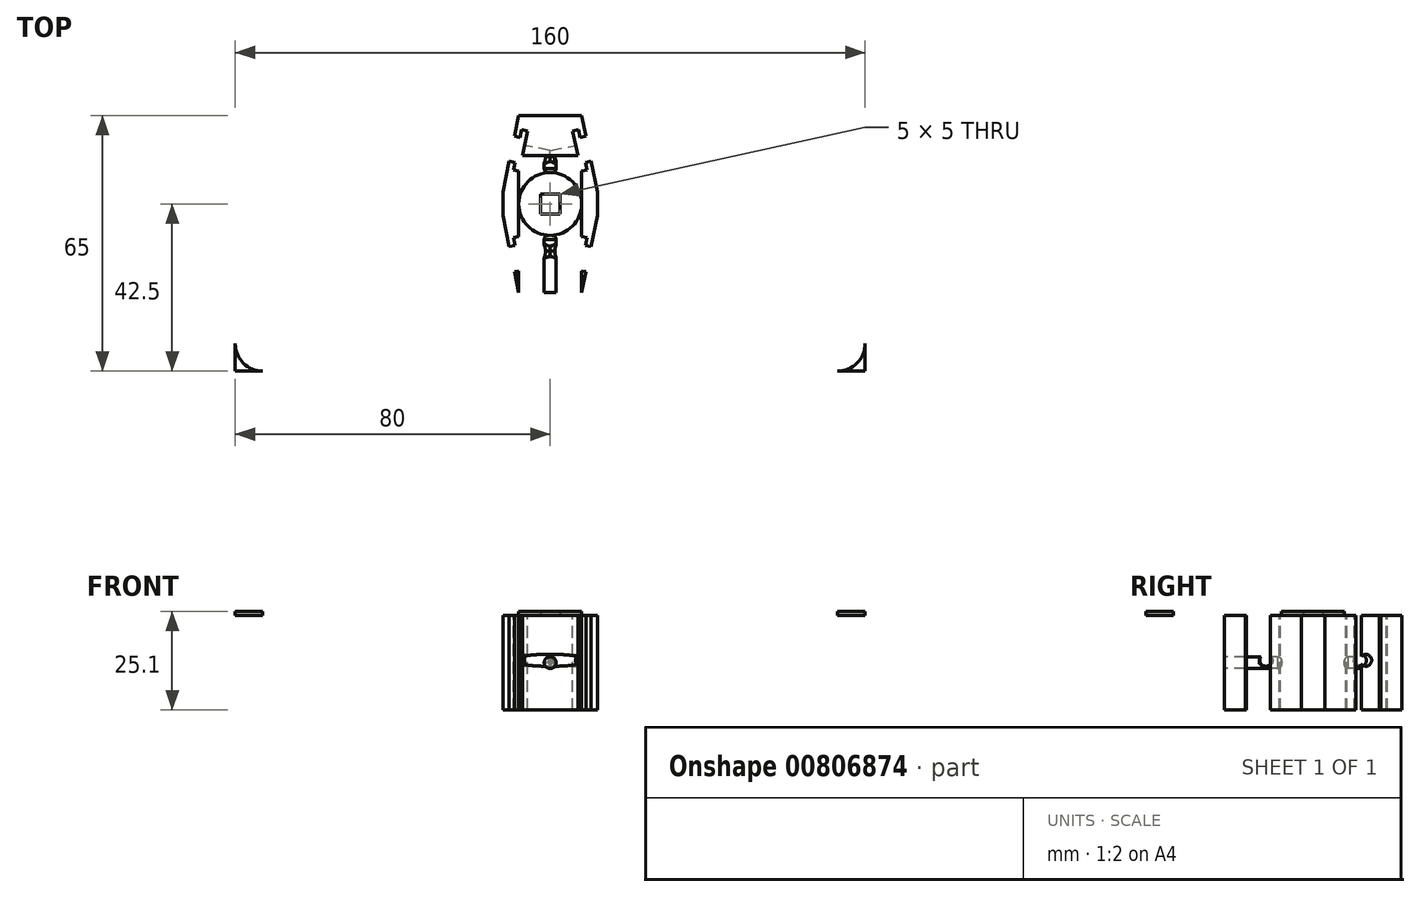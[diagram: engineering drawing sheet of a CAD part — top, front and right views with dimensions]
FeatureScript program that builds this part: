
annotation { "Feature Type Name" : "Feature", "Feature Type Description" : "" }
export const myFeature = defineFeature(function(context is Context, id is Id, definition is map)
    precondition{}
    {
        {
            var Q0;
            Q0=qCreatedBy(makeId("Top.planeOp"),FACE);
            var sketch = newSketch(context, id + "F0", { "sketchPlane" : qUnion([Q0])});
            skLineSegment(sketch, "E0.bottom", {"start": v(80, -42.5) * mm, "end": v(-80, -42.5) * mm});
            skLineSegment(sketch, "E0.top", {"start": v(80, 42.5) * mm, "end": v(-80, 42.5) * mm});
            skLineSegment(sketch, "E0.left", {"start": v(80, -42.5) * mm, "end": v(80, 42.5) * mm});
            skLineSegment(sketch, "E0.right", {"start": v(-80, -42.5) * mm, "end": v(-80, 42.5) * mm});
            skPoint(sketch, "E0.middle", {"position": v(0, 0) * mm});
            skCircle(sketch, "E1", {"center": v(0, 0) * mm, "radius": 8 * mm});
            skLineSegment(sketch, "E2", {"start": v(80, 42.5) * mm, "end": v(80, 35.5) * mm});
            skLineSegment(sketch, "E3", {"start": v(80, 42.5) * mm, "end": v(73, 42.5) * mm});
            skArc(sketch, "E4", {"start": v(80, 35.5) * mm, "mid": v(77.95, 40.45) * mm, "end": v(73, 42.5) * mm});
            skLineSegment(sketch, "E5", {"start": v(80, -42.5) * mm, "end": v(80, -35.5) * mm});
            skLineSegment(sketch, "E6", {"start": v(80, -42.5) * mm, "end": v(73, -42.5) * mm});
            skArc(sketch, "E7", {"start": v(73, -42.5) * mm, "mid": v(77.95, -40.45) * mm, "end": v(80, -35.5) * mm});
            skLineSegment(sketch, "E8", {"start": v(-80, -42.5) * mm, "end": v(-73, -42.5) * mm});
            skLineSegment(sketch, "E9", {"start": v(-80, -42.5) * mm, "end": v(-80, -35.5) * mm});
            skArc(sketch, "E10", {"start": v(-80, -35.5) * mm, "mid": v(-77.95, -40.45) * mm, "end": v(-73, -42.5) * mm});
            skLineSegment(sketch, "E11", {"start": v(-80, 42.5) * mm, "end": v(-80, 35.5) * mm});
            skLineSegment(sketch, "E12", {"start": v(-80, 42.5) * mm, "end": v(-73, 42.5) * mm});
            skArc(sketch, "E13", {"start": v(-73, 42.5) * mm, "mid": v(-77.95, 40.45) * mm, "end": v(-80, 35.5) * mm});
            skSolve(sketch);
        }
        {
            var Q0;
            Q0=makeQuery(id+"F0.imprint","IMPRINT",FACE,{"disambiguationData":[TD([[makeQuery(id+"F0.imprint","IMPRINT",EDGE,{"derivedFrom":sQuery(id+"F0.wireOp",EDGE,"E1")}),1.0]])]});
            var Q1;
            Q1=makeQuery(id+"F0.imprint","IMPRINT",FACE,{"disambiguationData":[TD([[makeQuery(id+"F0.imprint","IMPRINT",EDGE,{"derivedFrom":sQuery(id+"F0.wireOp",EDGE,"E0.bottom")}),-1.0]])]});
            extrude(context, id + "F1", {"entities" : qUnion([Q0, Q1]), "depth" : 1 * mm, "offsetDistance" : 25 * mm});
        }
        {
            var Q0;
            Q0=makeQuery(id+"F1.opExtrude","CAP_FACE",FACE,{"disambiguationData":[OSD([sQuery(id+"F0.wireOp",EDGE,"E0.bottom"),sQuery(id+"F0.wireOp",EDGE,"E0.top"),sQuery(id+"F0.wireOp",EDGE,"E0.left"),sQuery(id+"F0.wireOp",EDGE,"E0.right")])],"isStart":true});
            var sketch = newSketch(context, id + "F2", { "sketchPlane" : qUnion([Q0])});
            skCircle(sketch, "E14", {"center": v(0, 0) * mm, "radius": 8 * mm});
            skSolve(sketch);
        }
        {
            var Q0;
            Q0=makeQuery(id+"F1.opExtrude","CAP_FACE",FACE,{"disambiguationData":[OSD([sQuery(id+"F0.wireOp",EDGE,"E0.bottom"),sQuery(id+"F0.wireOp",EDGE,"E0.top"),sQuery(id+"F0.wireOp",EDGE,"E0.left"),sQuery(id+"F0.wireOp",EDGE,"E0.right")])],"isStart":true});
            var sketch = newSketch(context, id + "F3", { "sketchPlane" : qUnion([Q0])});
            skLineSegment(sketch, "E15", {"start": v(80, -42.5) * mm, "end": v(80, -3) * mm});
            skLineSegment(sketch, "E16", {"start": v(80, 42.5) * mm, "end": v(80, 3) * mm});
            skLineSegment(sketch, "E17", {"start": v(-80, 42.5) * mm, "end": v(-80, 3) * mm});
            skLineSegment(sketch, "E18", {"start": v(-80, -42.5) * mm, "end": v(-80, -3) * mm});
            skLineSegment(sketch, "E19", {"start": v(-80, 3) * mm, "end": v(-12, 3) * mm});
            skLineSegment(sketch, "E20", {"start": v(-80, -3) * mm, "end": v(-12, -3) * mm});
            skLineSegment(sketch, "E21", {"start": v(80, 3) * mm, "end": v(12, 3) * mm});
            skLineSegment(sketch, "E22", {"start": v(80, -3) * mm, "end": v(12, -3) * mm});
            skLineSegment(sketch, "E23", {"start": v(-12, 3) * mm, "end": v(-12, -3) * mm});
            skLineSegment(sketch, "E24", {"start": v(12, 3) * mm, "end": v(12, -3) * mm});
            skLineSegment(sketch, "E25", {"start": v(-8, -42.5) * mm, "end": v(73, -42.5) * mm});
            skLineSegment(sketch, "E26", {"start": v(8, -42.5) * mm, "end": v(73, -42.5) * mm});
            skLineSegment(sketch, "E27", {"start": v(-8, 42.5) * mm, "end": v(73, 42.5) * mm});
            skLineSegment(sketch, "E28", {"start": v(8, 42.5) * mm, "end": v(73, 42.5) * mm});
            skLineSegment(sketch, "E29", {"start": v(-8, 42.5) * mm, "end": v(-8, 22.5) * mm});
            skLineSegment(sketch, "E30", {"start": v(8, 42.5) * mm, "end": v(8, 22.5) * mm});
            skLineSegment(sketch, "E31", {"start": v(-8, -42.5) * mm, "end": v(-8, -22.5) * mm});
            skLineSegment(sketch, "E32", {"start": v(8, -42.5) * mm, "end": v(8, -22.5) * mm});
            skLineSegment(sketch, "E33", {"start": v(-8, -22.5) * mm, "end": v(8, -22.5) * mm});
            skLineSegment(sketch, "E34", {"start": v(-8, 22.5) * mm, "end": v(8, 22.5) * mm});
            skLineSegment(sketch, "E35", {"start": v(8, 22.5) * mm, "end": v(12, 3) * mm});
            skLineSegment(sketch, "E36", {"start": v(12, -3) * mm, "end": v(8, -22.5) * mm});
            skLineSegment(sketch, "E37", {"start": v(-8, -22.5) * mm, "end": v(-12, -3) * mm});
            skLineSegment(sketch, "E38", {"start": v(-8, 22.5) * mm, "end": v(-12, 3) * mm});
            skLineSegment(sketch, "E39", {"start": v(12, 3) * mm, "end": v(11.2, 6.92) * mm});
            skLineSegment(sketch, "E40", {"start": v(12, 3) * mm, "end": v(10.4, 10.84) * mm});
            skLineSegment(sketch, "E41", {"start": v(12, 3) * mm, "end": v(9.09, 17.2) * mm});
            skLineSegment(sketch, "E42", {"start": v(12, 3) * mm, "end": v(9.39, 15.73) * mm});
            skLineSegment(sketch, "E43", {"start": v(9.09, 17.2) * mm, "end": v(7.62, 16.9) * mm});
            skLineSegment(sketch, "E44", {"start": v(7.62, 16.9) * mm, "end": v(7.22, 18.86) * mm});
            skLineSegment(sketch, "E45", {"start": v(7.22, 18.86) * mm, "end": v(5.75, 18.56) * mm});
            skLineSegment(sketch, "E46", {"start": v(10.4, 10.84) * mm, "end": v(8.92, 10.54) * mm});
            skLineSegment(sketch, "E47", {"start": v(8.92, 10.54) * mm, "end": v(9.32, 8.58) * mm});
            skLineSegment(sketch, "E48", {"start": v(9.32, 8.58) * mm, "end": v(7.86, 8.27) * mm});
            skLineSegment(sketch, "E49", {"start": v(7.86, 8.27) * mm, "end": v(5.75, 18.56) * mm});
            skLineSegment(sketch, "E50", {"start": v(-12, 3) * mm, "end": v(-11.2, 6.92) * mm});
            skLineSegment(sketch, "E51", {"start": v(-12, 3) * mm, "end": v(-10.4, 10.84) * mm});
            skLineSegment(sketch, "E52", {"start": v(-12, 3) * mm, "end": v(-9.09, 17.2) * mm});
            skLineSegment(sketch, "E53", {"start": v(-12, 3) * mm, "end": v(-9.39, 15.73) * mm});
            skLineSegment(sketch, "E54", {"start": v(-10.4, 10.84) * mm, "end": v(-8.92, 10.54) * mm});
            skLineSegment(sketch, "E55", {"start": v(-8.92, 10.54) * mm, "end": v(-9.32, 8.58) * mm});
            skLineSegment(sketch, "E56", {"start": v(-9.32, 8.58) * mm, "end": v(-7.86, 8.27) * mm});
            skLineSegment(sketch, "E57", {"start": v(-9.09, 17.2) * mm, "end": v(-7.62, 16.9) * mm});
            skLineSegment(sketch, "E58", {"start": v(-7.62, 16.9) * mm, "end": v(-7.22, 18.86) * mm});
            skLineSegment(sketch, "E59", {"start": v(-7.22, 18.86) * mm, "end": v(-5.75, 18.56) * mm});
            skLineSegment(sketch, "E60", {"start": v(-5.75, 18.56) * mm, "end": v(-7.86, 8.27) * mm});
            skLineSegment(sketch, "E61", {"start": v(12, -3) * mm, "end": v(10.8, -8.88) * mm});
            skLineSegment(sketch, "E62", {"start": v(12, -3) * mm, "end": v(10.4, -10.84) * mm});
            skLineSegment(sketch, "E63", {"start": v(12, -3) * mm, "end": v(9.09, -17.2) * mm});
            skLineSegment(sketch, "E64", {"start": v(12, -3) * mm, "end": v(8.99, -17.7) * mm});
            skLineSegment(sketch, "E65", {"start": v(10.4, -10.84) * mm, "end": v(8.92, -10.54) * mm});
            skLineSegment(sketch, "E66", {"start": v(8.92, -10.54) * mm, "end": v(9.32, -8.58) * mm});
            skLineSegment(sketch, "E67", {"start": v(9.32, -8.58) * mm, "end": v(7.86, -8.27) * mm});
            skLineSegment(sketch, "E68", {"start": v(9.09, -17.2) * mm, "end": v(7.62, -16.9) * mm});
            skLineSegment(sketch, "E69", {"start": v(7.62, -16.9) * mm, "end": v(7.22, -18.86) * mm});
            skLineSegment(sketch, "E70", {"start": v(7.22, -18.86) * mm, "end": v(5.75, -18.56) * mm});
            skLineSegment(sketch, "E71", {"start": v(5.75, -18.56) * mm, "end": v(7.86, -8.27) * mm});
            skLineSegment(sketch, "E72", {"start": v(-12, -3) * mm, "end": v(-11.2, -6.92) * mm});
            skLineSegment(sketch, "E73", {"start": v(-12, -3) * mm, "end": v(-10.4, -10.84) * mm});
            skLineSegment(sketch, "E74", {"start": v(-12, -3) * mm, "end": v(-9.09, -17.2) * mm});
            skLineSegment(sketch, "E75", {"start": v(-12, -3) * mm, "end": v(-9.39, -15.73) * mm});
            skLineSegment(sketch, "E76", {"start": v(-10.4, -10.84) * mm, "end": v(-8.92, -10.54) * mm});
            skLineSegment(sketch, "E77", {"start": v(-8.92, -10.54) * mm, "end": v(-9.32, -8.58) * mm});
            skLineSegment(sketch, "E78", {"start": v(-9.32, -8.58) * mm, "end": v(-7.86, -8.27) * mm});
            skLineSegment(sketch, "E79", {"start": v(-9.09, -17.2) * mm, "end": v(-7.62, -16.9) * mm});
            skLineSegment(sketch, "E80", {"start": v(-7.62, -16.9) * mm, "end": v(-7.22, -18.86) * mm});
            skLineSegment(sketch, "E81", {"start": v(-7.22, -18.86) * mm, "end": v(-5.75, -18.56) * mm});
            skLineSegment(sketch, "E82", {"start": v(-5.75, -18.56) * mm, "end": v(-7.86, -8.27) * mm});
            skCircle(sketch, "E83", {"center": v(0, 0) * mm, "radius": 8 * mm});
            skLineSegment(sketch, "E84", {"start": v(9.09, 17.2) * mm, "end": v(10.4, 10.84) * mm});
            skLineSegment(sketch, "E85", {"start": v(10.4, -10.84) * mm, "end": v(9.09, -17.2) * mm});
            skLineSegment(sketch, "E86", {"start": v(-10.4, -10.84) * mm, "end": v(-9.09, -17.2) * mm});
            skSolve(sketch);
        }
        {
            var Q0;
            {var subQ5=sQuery(id+"F3.wireOp",EDGE,"E23");Q0=makeQuery(id+"F3.imprint","IMPRINT",FACE,{"disambiguationData":[TD([[makeQuery(id+"F3.imprint","IMPRINT",EDGE,{"derivedFrom":subQ5}),1.0]])]});}
            extrude(context, id + "F4", {"entities" : qUnion([Q0]), "operationType" : NewBodyOperationType.ADD, "depth" : 24.1 * mm, "offsetDistance" : 25 * mm});
        }
        {
            var Q0;
            Q0=makeQuery(id+"F4.opExtrude","CAP_FACE",FACE,{"disambiguationData":[OSD([sQuery(id+"F3.wireOp",EDGE,"E23"),sQuery(id+"F3.wireOp",EDGE,"E24"),sQuery(id+"F3.wireOp",EDGE,"E33"),sQuery(id+"F3.wireOp",EDGE,"E34"),sQuery(id+"F3.wireOp",EDGE,"E35"),sQuery(id+"F3.wireOp",EDGE,"E36"),sQuery(id+"F3.wireOp",EDGE,"E37"),sQuery(id+"F3.wireOp",EDGE,"E38"),sQuery(id+"F3.wireOp",EDGE,"E42"),sQuery(id+"F3.wireOp",EDGE,"E43"),sQuery(id+"F3.wireOp",EDGE,"E44"),sQuery(id+"F3.wireOp",EDGE,"E45"),sQuery(id+"F3.wireOp",EDGE,"E46"),sQuery(id+"F3.wireOp",EDGE,"E47"),sQuery(id+"F3.wireOp",EDGE,"E48"),sQuery(id+"F3.wireOp",EDGE,"E49"),sQuery(id+"F3.wireOp",EDGE,"E53"),sQuery(id+"F3.wireOp",EDGE,"E54"),sQuery(id+"F3.wireOp",EDGE,"E55"),sQuery(id+"F3.wireOp",EDGE,"E56"),sQuery(id+"F3.wireOp",EDGE,"E57"),sQuery(id+"F3.wireOp",EDGE,"E58"),sQuery(id+"F3.wireOp",EDGE,"E59"),sQuery(id+"F3.wireOp",EDGE,"E60"),sQuery(id+"F3.wireOp",EDGE,"E64"),sQuery(id+"F3.wireOp",EDGE,"E65"),sQuery(id+"F3.wireOp",EDGE,"E66"),sQuery(id+"F3.wireOp",EDGE,"E67"),sQuery(id+"F3.wireOp",EDGE,"E68"),sQuery(id+"F3.wireOp",EDGE,"E69"),sQuery(id+"F3.wireOp",EDGE,"E70"),sQuery(id+"F3.wireOp",EDGE,"E71"),sQuery(id+"F3.wireOp",EDGE,"E75"),sQuery(id+"F3.wireOp",EDGE,"E76"),sQuery(id+"F3.wireOp",EDGE,"E77"),sQuery(id+"F3.wireOp",EDGE,"E78"),sQuery(id+"F3.wireOp",EDGE,"E79"),sQuery(id+"F3.wireOp",EDGE,"E80"),sQuery(id+"F3.wireOp",EDGE,"E81"),sQuery(id+"F3.wireOp",EDGE,"E82"),sQuery(id+"F3.wireOp",EDGE,"E83")])],"isStart":false});
            var sketch = newSketch(context, id + "F5", { "sketchPlane" : qUnion([Q0])});
            skLineSegment(sketch, "E87", {"start": v(8, -22.5) * mm, "end": v(-8, -22.5) * mm});
            skLineSegment(sketch, "E88", {"start": v(8, -22.5) * mm, "end": v(8.4, -20.54) * mm});
            skLineSegment(sketch, "E89", {"start": v(-8, -22.5) * mm, "end": v(-8.4, -20.54) * mm});
            skLineSegment(sketch, "E90", {"start": v(-8.4, -20.54) * mm, "end": v(8.4, -20.54) * mm});
            skSolve(sketch);
        }
        {
            var Q0;
            Q0=makeQuery(id+"F4.opExtrude","SWEPT_FACE",FACE,{"disambiguationData":[OSD([sQuery(id+"F3.wireOp",EDGE,"E71")])]});
            var sketch = newSketch(context, id + "F6", { "sketchPlane" : qUnion([Q0])});
            skLineSegment(sketch, "E91", {"start": v(11.78, 0) * mm, "end": v(11.78, -11.45) * mm});
            skCircle(sketch, "E92", {"center": v(11.78, -11.45) * mm, "radius": 1.5 * mm});
            skSolve(sketch);
        }
        {
            var Q0;
            Q0=makeQuery(id+"F6.imprint","IMPRINT",FACE,{"disambiguationData":[TD([[makeQuery(id+"F6.imprint","IMPRINT",EDGE,{"derivedFrom":sQuery(id+"F6.wireOp",EDGE,"E92")}),1.0]])]});
            var Q1;
            Q1=sQuery(id+"F6.wireOp",EDGE,"E92");
            extrude(context, id + "F7", {"entities" : qUnion([Q0]), "operationType" : NewBodyOperationType.REMOVE, "surfaceEntities" : qUnion([Q1]), "oppositeDirection" : true, "depth" : 8.71 * mm, "offsetDistance" : 25 * mm});
        }
        {
            var Q0;
            Q0=makeQuery(id+"F4.opExtrude","SWEPT_FACE",FACE,{"disambiguationData":[OSD([sQuery(id+"F3.wireOp",EDGE,"E82")])]});
            var sketch = newSketch(context, id + "F8", { "sketchPlane" : qUnion([Q0])});
            skLineSegment(sketch, "E93", {"start": v(-11.78, 0) * mm, "end": v(-11.78, -11.45) * mm});
            skCircle(sketch, "E94", {"center": v(-11.78, -11.45) * mm, "radius": 1.5 * mm});
            skSolve(sketch);
        }
        {
            var Q0;
            Q0=makeQuery(id+"F8.imprint","IMPRINT",FACE,{"disambiguationData":[TD([[makeQuery(id+"F8.imprint","IMPRINT",EDGE,{"derivedFrom":sQuery(id+"F8.wireOp",EDGE,"E94")}),1.0]])]});
            var Q1;
            Q1=sQuery(id+"F8.wireOp",EDGE,"E94");
            extrude(context, id + "F9", {"entities" : qUnion([Q0]), "operationType" : NewBodyOperationType.REMOVE, "surfaceEntities" : qUnion([Q1]), "oppositeDirection" : true, "depth" : 8.18 * mm, "offsetDistance" : 25 * mm});
        }
        {
            var Q0;
            Q0=makeQuery(id+"F4.opExtrude","SWEPT_FACE",FACE,{"disambiguationData":[OSD([sQuery(id+"F3.wireOp",EDGE,"E60")])]});
            var sketch = newSketch(context, id + "F10", { "sketchPlane" : qUnion([Q0])});
            skLineSegment(sketch, "E95", {"start": v(11.78, 0) * mm, "end": v(11.78, -11.45) * mm});
            skCircle(sketch, "E96", {"center": v(11.78, -11.45) * mm, "radius": 1.5 * mm});
            skSolve(sketch);
        }
        {
            var Q0;
            Q0=qSketchRegion(id+"F10",true);
            extrude(context, id + "F11", {"entities" : qUnion([Q0]), "operationType" : NewBodyOperationType.REMOVE, "oppositeDirection" : true, "depth" : 8.71 * mm, "offsetDistance" : 25 * mm});
        }
        {
            var Q0;
            Q0=makeQuery(id+"F4.opExtrude","SWEPT_FACE",FACE,{"disambiguationData":[OSD([sQuery(id+"F3.wireOp",EDGE,"E49")])]});
            var sketch = newSketch(context, id + "F12", { "sketchPlane" : qUnion([Q0])});
            skLineSegment(sketch, "E97", {"start": v(-11.78, 0) * mm, "end": v(-11.78, -11.45) * mm});
            skCircle(sketch, "E98", {"center": v(-11.78, -11.45) * mm, "radius": 1.5 * mm});
            skSolve(sketch);
        }
        {
            var Q0;
            Q0=qSketchRegion(id+"F12",true);
            extrude(context, id + "F13", {"entities" : qUnion([Q0]), "operationType" : NewBodyOperationType.REMOVE, "oppositeDirection" : true, "depth" : 8.71 * mm, "offsetDistance" : 25 * mm});
        }
        {
            var Q0;
            Q0=makeQuery(id+"F4.boolean.opBoolean","SPLIT",FACE,{"disambiguationData":[TD([makeQuery(id+"F4.opExtrude","SWEPT_FACE",FACE,{"disambiguationData":[OSD([sQuery(id+"F3.wireOp",EDGE,"E83")])]})])],"derivedFrom":makeQuery(id+"F1.opExtrude","CAP_FACE",FACE,{"disambiguationData":[OSD([sQuery(id+"F0.wireOp",EDGE,"E0.bottom"),sQuery(id+"F0.wireOp",EDGE,"E0.top"),sQuery(id+"F0.wireOp",EDGE,"E0.left"),sQuery(id+"F0.wireOp",EDGE,"E0.right")])],"isStart":true})});
            var sketch = newSketch(context, id + "F14", { "sketchPlane" : qUnion([Q0])});
            skLineSegment(sketch, "E99.bottom", {"start": v(2.5, -2.5) * mm, "end": v(-2.5, -2.5) * mm});
            skLineSegment(sketch, "E99.top", {"start": v(2.5, 2.5) * mm, "end": v(-2.5, 2.5) * mm});
            skLineSegment(sketch, "E99.left", {"start": v(2.5, -2.5) * mm, "end": v(2.5, 2.5) * mm});
            skLineSegment(sketch, "E99.right", {"start": v(-2.5, -2.5) * mm, "end": v(-2.5, 2.5) * mm});
            skPoint(sketch, "E99.middle", {"position": v(0, 0) * mm});
            skSolve(sketch);
        }
        {
            var Q0;
            Q0=qSketchRegion(id+"F14",true);
            extrude(context, id + "F15", {"entities" : qUnion([Q0]), "operationType" : NewBodyOperationType.REMOVE, "oppositeDirection" : true, "depth" : 25 * mm, "offsetDistance" : 25 * mm});
        }
        {
            var Q0;
            Q0=makeQuery(id+"F4.opExtrude","SWEPT_FACE",FACE,{"disambiguationData":[OSD([sQuery(id+"F3.wireOp",EDGE,"E34")])]});
            var sketch = newSketch(context, id + "F16", { "sketchPlane" : qUnion([Q0])});
            skLineSegment(sketch, "E100", {"start": v(0, -24.1) * mm, "end": v(0, 0) * mm});
            skLineSegment(sketch, "E101", {"start": v(0, 0) * mm, "end": v(0, -12.05) * mm});
            skCircle(sketch, "E102", {"center": v(0, -12.05) * mm, "radius": 1.5 * mm});
            skSolve(sketch);
        }
        {
            var Q0;
            {var subQ0=sQuery(id+"F16.wireOp",EDGE,"E101");var subQ1=sQuery(id+"F16.wireOp",EDGE,"E100");var subQ2=makeQuery(id+"F16.imprint","INTERSECT",VERTEX,{"derivedFrom":[subQ1,subQ0]});Q0=makeQuery(id+"F16.imprint","IMPRINT",FACE,{"disambiguationData":[TD([[makeQuery(id+"F16.imprint","IMPRINT",EDGE,{"disambiguationData":[TD([[subQ2,1.0]])],"derivedFrom":subQ1}),1.0]])]});}
            var Q1;
            {var subQ0=sQuery(id+"F16.wireOp",EDGE,"E101");var subQ1=sQuery(id+"F16.wireOp",EDGE,"E100");var subQ2=makeQuery(id+"F16.imprint","INTERSECT",VERTEX,{"derivedFrom":[subQ1,subQ0]});Q1=makeQuery(id+"F16.imprint","IMPRINT",FACE,{"disambiguationData":[TD([[makeQuery(id+"F16.imprint","IMPRINT",EDGE,{"disambiguationData":[TD([[subQ2,1.0]])],"derivedFrom":subQ1}),-1.0]])]});}
            var Q2;
            Q2=sQuery(id+"F16.wireOp",EDGE,"E102");
            extrude(context, id + "F17", {"entities" : qUnion([Q0, Q1]), "operationType" : NewBodyOperationType.REMOVE, "surfaceEntities" : qUnion([Q2]), "oppositeDirection" : true, "depth" : 34.8 * mm, "offsetDistance" : 25 * mm});
        }
        {
            var Q0;
            Q0=makeQuery(id+"F17.boolean.opBoolean","INTERSECT",EDGE,{"disambiguationData":[OD(0.0)],"derivedFrom":[makeQuery(id+"F4.opExtrude","SWEPT_FACE",FACE,{"disambiguationData":[OSD([sQuery(id+"F3.wireOp",EDGE,"E83")])]}),makeQuery(id+"F17.opExtrude","SWEPT_FACE",FACE,{"disambiguationData":[OSD([sQuery(id+"F16.wireOp",EDGE,"E102")])]})]});
            fillet(context, id + "F18", {"entities" : qUnion([Q0]), "radius" : 1 * mm, "tangentPropagation" : true, "allowEdgeOverflow" : false});
        }
        {
            var Q0;
            Q0=makeQuery(id+"F17.boolean.opBoolean","INTERSECT",EDGE,{"disambiguationData":[OD(1.0)],"derivedFrom":[makeQuery(id+"F4.opExtrude","SWEPT_FACE",FACE,{"disambiguationData":[OSD([sQuery(id+"F3.wireOp",EDGE,"E83")])]}),makeQuery(id+"F17.opExtrude","SWEPT_FACE",FACE,{"disambiguationData":[OSD([sQuery(id+"F16.wireOp",EDGE,"E102")])]})]});
            fillet(context, id + "F19", {"entities" : qUnion([Q0]), "radius" : 1 * mm, "tangentPropagation" : true, "allowEdgeOverflow" : false});
        }
        {
            var Q0;
            Q0=makeQuery(id+"F4.opExtrude","SWEPT_FACE",FACE,{"disambiguationData":[OSD([sQuery(id+"F3.wireOp",EDGE,"E34")])]});
            var sketch = newSketch(context, id + "F20", { "sketchPlane" : qUnion([Q0])});
            skCircle(sketch, "E103", {"center": v(0, -12.05) * mm, "radius": 1.5 * mm});
            skSolve(sketch);
        }
        {
            var Q0;
            Q0=qSketchRegion(id+"F20",true);
            extrude(context, id + "F21", {"entities" : qUnion([Q0]), "operationType" : NewBodyOperationType.ADD, "oppositeDirection" : true, "depth" : 8.88 * mm, "offsetDistance" : 25 * mm});
        }
    });
